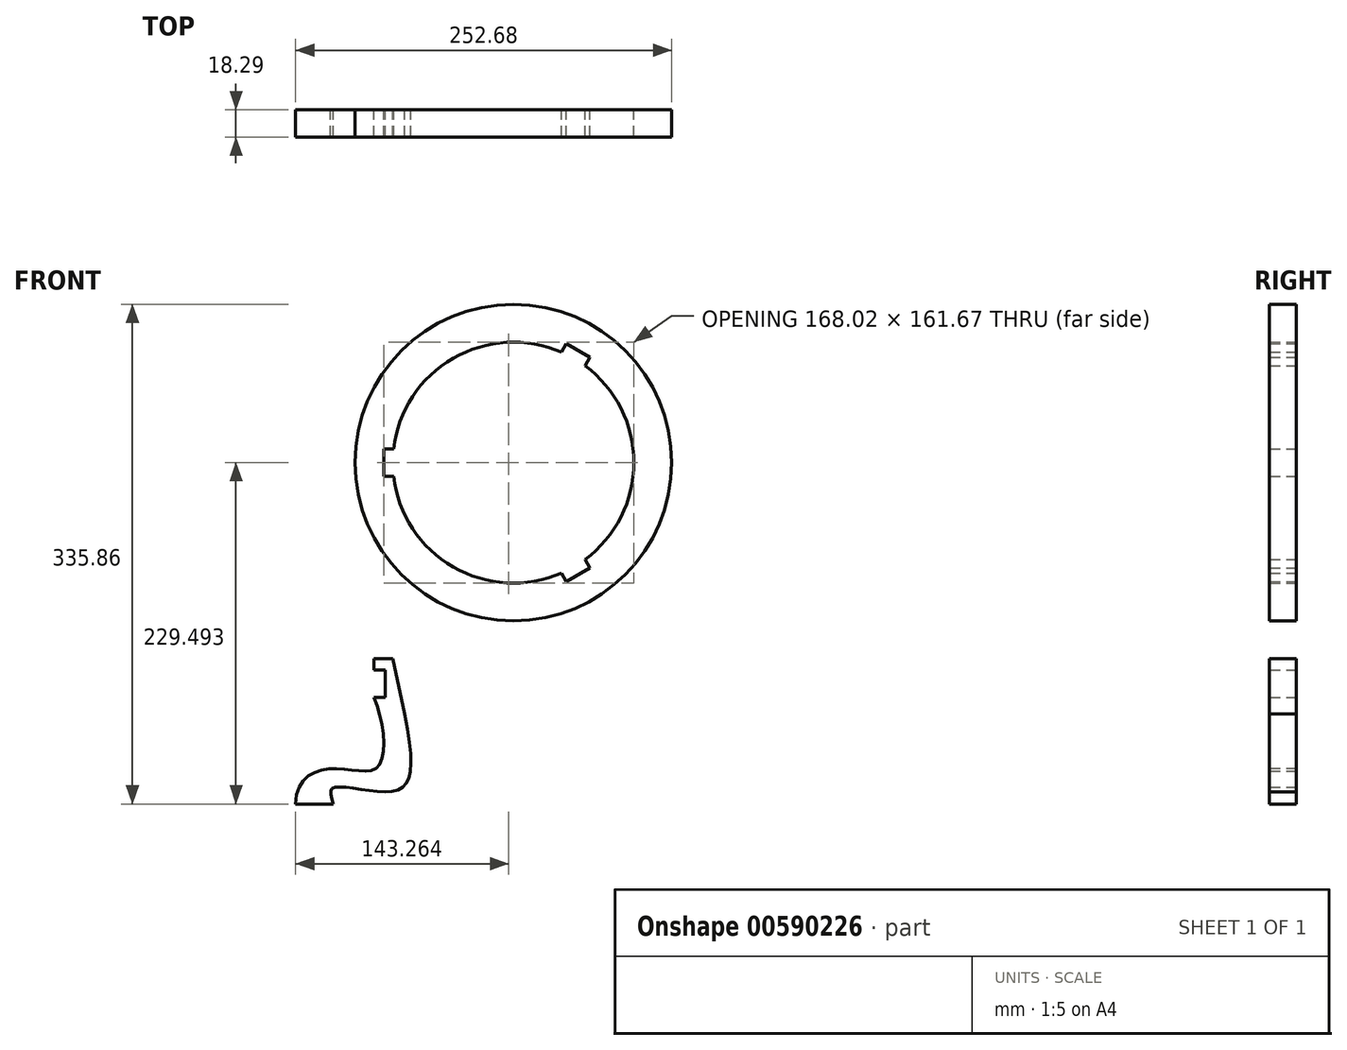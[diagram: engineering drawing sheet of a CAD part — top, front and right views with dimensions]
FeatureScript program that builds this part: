
annotation { "Feature Type Name" : "Feature", "Feature Type Description" : "" }
export const myFeature = defineFeature(function(context is Context, id is Id, definition is map)
    precondition{}
    {
        {
            var Q0;
            Q0=qCreatedBy(makeId("Front.planeOp"),FACE);
            var sketch = newSketch(context, id + "F0", { "sketchPlane" : qUnion([Q0])});
            skLineSegment(sketch, "E0", {"start": v(0, 0) * mm, "end": v(8, -37.25) * mm});
            skLineSegment(sketch, "E1", {"start": v(0, 0) * mm, "end": v(-12.7, 0) * mm});
            skLineSegment(sketch, "E2", {"start": v(-12.7, 0) * mm, "end": v(-12.7, -7.62) * mm});
            skLineSegment(sketch, "E3", {"start": v(-12.7, -7.62) * mm, "end": v(-5.08, -7.62) * mm});
            skLineSegment(sketch, "E4", {"start": v(-5.08, -7.62) * mm, "end": v(-5.08, -25.9) * mm});
            skLineSegment(sketch, "E5", {"start": v(-5.08, -25.9) * mm, "end": v(-12.7, -25.9) * mm});
            skFitSpline(sketch, "E6", {"points": [v(-12.7, -25.9) * mm, v(-10.35, -72.87) * mm, v(-41.05, -73.83) * mm, v(-65.35, -97.73) * mm], "startDerivative": vector(51.79, -125.62) * mm, "endDerivative": vector(0, -153.9) * mm});
            skLineSegment(sketch, "E7", {"start": v(-65.35, -97.73) * mm, "end": v(-39.95, -97.73) * mm});
            skFitSpline(sketch, "E8", {"points": [v(-39.95, -97.73) * mm, v(-39.95, -86.77) * mm, v(0, -89.08) * mm, v(8, -37.25) * mm], "startDerivative": vector(-27.22, 87.41) * mm, "endDerivative": vector(-47.94, 245.15) * mm});
            skLineSegment(sketch, "E9", {"start": v(0, 0) * mm, "end": v(161.93, 0) * mm, "construction": true});
            skCircle(sketch, "E10", {"center": v(80.96, 131.76) * mm, "radius": 80.96 * mm});
            skPoint(sketch, "E10.centerSnap0", {"position": v(80.96, 0) * mm});
            skLineSegment(sketch, "E11.bottom", {"start": v(-6.1, 122.62) * mm, "end": v(0, 122.62) * mm});
            skLineSegment(sketch, "E11.top", {"start": v(-6.1, 140.9) * mm, "end": v(0, 140.9) * mm});
            skLineSegment(sketch, "E11.left", {"start": v(-6.1, 122.62) * mm, "end": v(-6.1, 140.9) * mm});
            skLineSegment(sketch, "E11.right", {"start": v(0, 122.62) * mm, "end": v(0, 140.9) * mm});
            skPoint(sketch, "E12", {"position": v(0, 131.76) * mm});
            skLineSegment(sketch, "E13", {"start": v(0, 140.9) * mm, "end": v(0.52, 140.9) * mm});
            skLineSegment(sketch, "E14", {"start": v(0, 122.62) * mm, "end": v(0.52, 122.62) * mm});
            skLineSegment(sketch, "E15.1.0", {"start": v(132.41, 60.94) * mm, "end": v(116.57, 51.8) * mm});
            skLineSegment(sketch, "E15.1.1", {"start": v(129.36, 66.22) * mm, "end": v(113.52, 57.07) * mm});
            skLineSegment(sketch, "E15.1.2", {"start": v(132.41, 60.94) * mm, "end": v(129.36, 66.22) * mm});
            skLineSegment(sketch, "E15.1.3", {"start": v(116.57, 51.8) * mm, "end": v(113.52, 57.07) * mm});
            skPoint(sketch, "E15.1.4", {"position": v(121.44, 61.65) * mm});
            skLineSegment(sketch, "E15.1.5", {"start": v(113.52, 57.07) * mm, "end": v(113.27, 57.52) * mm});
            skLineSegment(sketch, "E15.1.6", {"start": v(129.36, 66.22) * mm, "end": v(129.1, 66.67) * mm});
            skLineSegment(sketch, "E15.2.0", {"start": v(116.57, 211.73) * mm, "end": v(132.41, 202.59) * mm});
            skLineSegment(sketch, "E15.2.1", {"start": v(113.52, 206.45) * mm, "end": v(129.36, 197.3) * mm});
            skLineSegment(sketch, "E15.2.2", {"start": v(116.57, 211.73) * mm, "end": v(113.52, 206.45) * mm});
            skLineSegment(sketch, "E15.2.3", {"start": v(132.41, 202.59) * mm, "end": v(129.36, 197.3) * mm});
            skPoint(sketch, "E15.2.4", {"position": v(121.44, 201.88) * mm});
            skLineSegment(sketch, "E15.2.5", {"start": v(129.36, 197.3) * mm, "end": v(129.1, 196.86) * mm});
            skLineSegment(sketch, "E15.2.6", {"start": v(113.52, 206.45) * mm, "end": v(113.27, 206) * mm});
            skCircle(sketch, "E16", {"center": v(80.96, 131.76) * mm, "radius": 106.36 * mm});
            skSolve(sketch);
        }
        {
            var Q0;
            Q0=makeQuery(id+"F0.imprint","IMPRINT",FACE,{"disambiguationData":[TD([[makeQuery(id+"F0.imprint","IMPRINT",EDGE,{"derivedFrom":sQuery(id+"F0.wireOp",EDGE,"E11.bottom")}),-1.0]])]});
            var Q1;
            Q1=makeQuery(id+"F0.imprint","IMPRINT",FACE,{"disambiguationData":[TD([[makeQuery(id+"F0.imprint","IMPRINT",EDGE,{"derivedFrom":sQuery(id+"F0.wireOp",EDGE,"E0")}),-1.0]])]});
            extrude(context, id + "F1", {"entities" : qUnion([Q0, Q1]), "depth" : 18.29 * mm, "offsetDistance" : 25.4 * mm});
        }
    });
